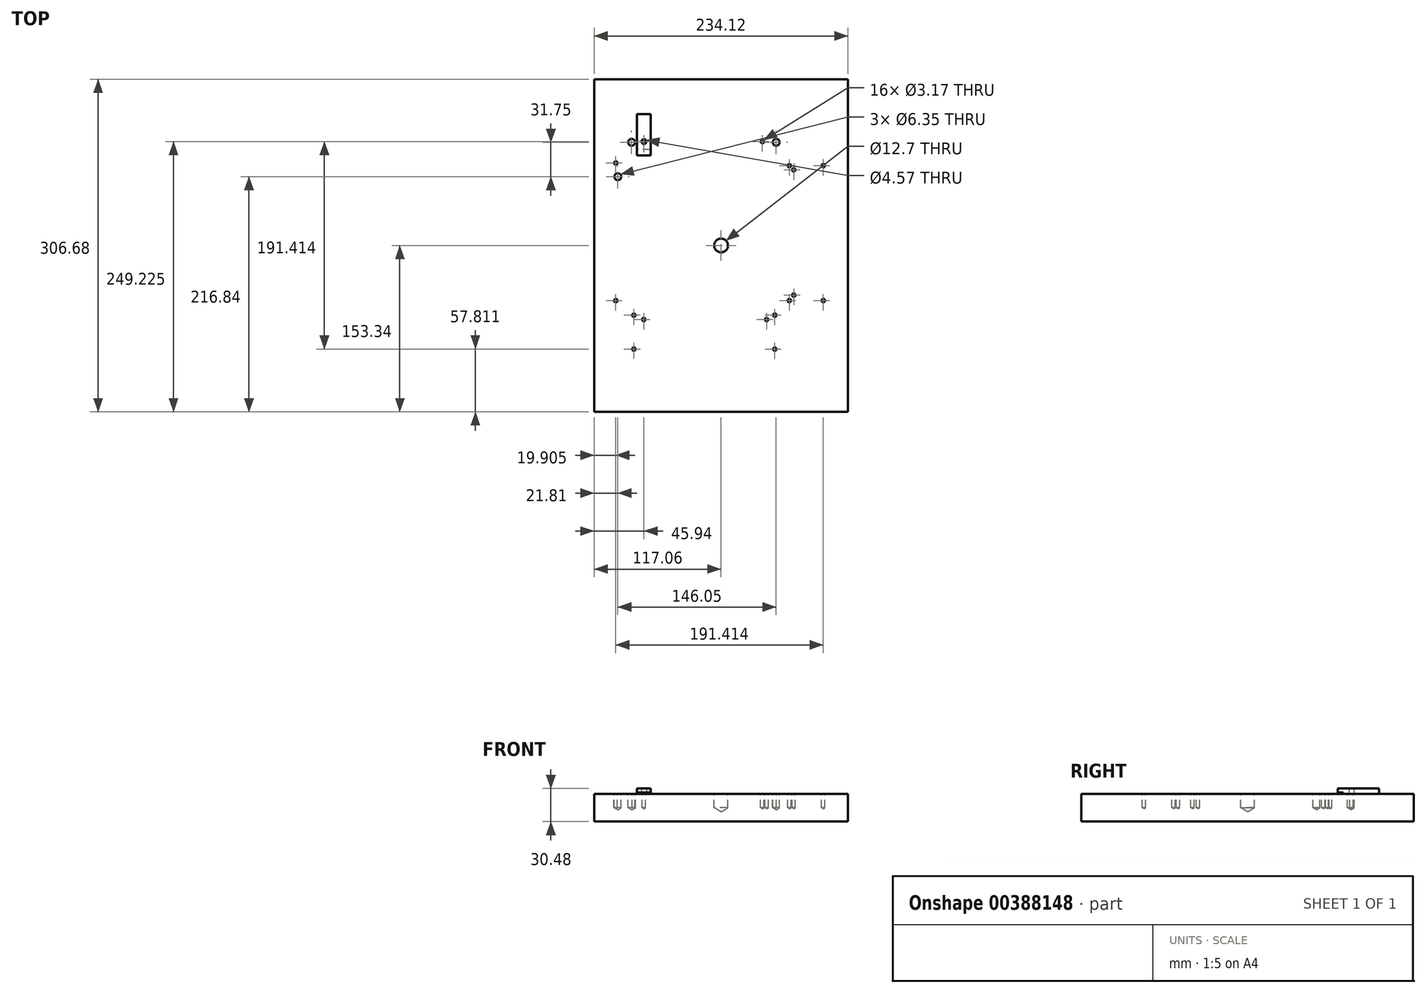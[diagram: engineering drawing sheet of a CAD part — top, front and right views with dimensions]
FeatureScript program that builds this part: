
annotation { "Feature Type Name" : "Feature", "Feature Type Description" : "" }
export const myFeature = defineFeature(function(context is Context, id is Id, definition is map)
    precondition{}
    {
        {
            var Q0;
            Q0=qCreatedBy(makeId("Top.planeOp"),FACE);
            var sketch = newSketch(context, id + "F0", { "sketchPlane" : qUnion([Q0])});
            skLineSegment(sketch, "E0.bottom", {"start": v(-117.06, 153.34) * mm, "end": v(117.06, 153.34) * mm});
            skLineSegment(sketch, "E0.top", {"start": v(-117.06, -153.34) * mm, "end": v(117.06, -153.34) * mm});
            skLineSegment(sketch, "E0.left", {"start": v(-117.06, 153.34) * mm, "end": v(-117.06, -153.34) * mm});
            skLineSegment(sketch, "E0.right", {"start": v(117.06, 153.34) * mm, "end": v(117.06, -153.34) * mm});
            skPoint(sketch, "E0.middle", {"position": v(0, 0) * mm});
            skPoint(sketch, "E1", {"position": v(-82.55, 95.25) * mm});
            skPoint(sketch, "E2", {"position": v(50.8, 95.25) * mm});
            skPoint(sketch, "E3", {"position": v(-95.25, 63.5) * mm});
            skPoint(sketch, "E4", {"position": v(-71.12, 95.88) * mm});
            skPoint(sketch, "E5", {"position": v(38.1, 95.89) * mm});
            skPoint(sketch, "E6", {"position": v(-97.16, 76.2) * mm});
            skPoint(sketch, "E7", {"position": v(-97.15, -50.8) * mm});
            skLineSegment(sketch, "E8", {"start": v(-97.16, 76.2) * mm, "end": v(-97.16, -50.8) * mm, "construction": true});
            skLineSegment(sketch, "E9", {"start": v(-71.12, 95.88) * mm, "end": v(38.1, 95.89) * mm, "construction": true});
            skLineSegment(sketch, "E10", {"start": v(62.94, 73.66) * mm, "end": v(62.94, -50.8) * mm, "construction": true});
            skLineSegment(sketch, "E11", {"start": v(67, 69.85) * mm, "end": v(67, -45.72) * mm, "construction": true});
            skLineSegment(sketch, "E12", {"start": v(94.26, 73.66) * mm, "end": v(94.26, -50.8) * mm, "construction": true});
            skLineSegment(sketch, "E13.bottom", {"start": v(-89.18, 87.9) * mm, "end": v(86.28, 87.9) * mm, "construction": true});
            skLineSegment(sketch, "E13.top", {"start": v(-89.18, -87.55) * mm, "end": v(86.28, -87.55) * mm, "construction": true});
            skLineSegment(sketch, "E13.left", {"start": v(-89.18, 87.9) * mm, "end": v(-89.18, -87.55) * mm, "construction": true});
            skLineSegment(sketch, "E13.right", {"start": v(86.28, 87.9) * mm, "end": v(86.28, -87.55) * mm, "construction": true});
            skLineSegment(sketch, "E14", {"start": v(59.03, 87.9) * mm, "end": v(59.03, -60.3) * mm, "construction": true});
            skLineSegment(sketch, "E15", {"start": v(59.03, -60.3) * mm, "end": v(-89.18, -60.3) * mm, "construction": true});
            skLineSegment(sketch, "E16", {"start": v(54.97, 87.9) * mm, "end": v(54.97, -56.24) * mm, "construction": true});
            skLineSegment(sketch, "E17", {"start": v(54.97, -56.24) * mm, "end": v(-89.18, -56.24) * mm, "construction": true});
            skPoint(sketch, "E18", {"position": v(62.94, 73.66) * mm});
            skPoint(sketch, "E19", {"position": v(67, 69.85) * mm});
            skPoint(sketch, "E20", {"position": v(94.26, 73.66) * mm});
            skPoint(sketch, "E21", {"position": v(62.94, -50.8) * mm});
            skPoint(sketch, "E22", {"position": v(67, -45.72) * mm});
            skPoint(sketch, "E23", {"position": v(94.26, -50.8) * mm});
            skLineSegment(sketch, "E24", {"start": v(-80.47, -64.21) * mm, "end": v(49.5, -64.21) * mm, "construction": true});
            skLineSegment(sketch, "E25", {"start": v(-71.33, -68.28) * mm, "end": v(42.03, -68.28) * mm, "construction": true});
            skLineSegment(sketch, "E26", {"start": v(-80.47, -95.53) * mm, "end": v(49.5, -95.53) * mm, "construction": true});
            skPoint(sketch, "E27", {"position": v(-80.47, -95.53) * mm});
            skPoint(sketch, "E28", {"position": v(-71.33, -68.28) * mm});
            skPoint(sketch, "E29", {"position": v(-80.47, -64.21) * mm});
            skPoint(sketch, "E30", {"position": v(49.5, -64.21) * mm});
            skPoint(sketch, "E31", {"position": v(42.03, -68.28) * mm});
            skPoint(sketch, "E32", {"position": v(49.5, -95.53) * mm});
            skCircle(sketch, "E33", {"center": v(-92.35, 91.08) * mm, "radius": 3.18 * mm, "construction": true});
            skCircle(sketch, "E34", {"center": v(-92.35, -59.41) * mm, "radius": 3.18 * mm, "construction": true});
            skCircle(sketch, "E35", {"center": v(-92.35, -90.73) * mm, "radius": 3.18 * mm, "construction": true});
            skCircle(sketch, "E36", {"center": v(-92.35, -63.47) * mm, "radius": 3.18 * mm, "construction": true});
            skCircle(sketch, "E37", {"center": v(58.14, -59.41) * mm, "radius": 3.18 * mm, "construction": true});
            skCircle(sketch, "E38", {"center": v(62.2, -63.47) * mm, "radius": 3.18 * mm, "construction": true});
            skCircle(sketch, "E39", {"center": v(89.46, -90.73) * mm, "radius": 3.18 * mm, "construction": true});
            skSolve(sketch);
        }
        {
            var Q0;
            Q0 = qSketchRegion(id + "F0", true);
            extrude(context, id + "F1", {"entities" : qUnion([Q0]), "oppositeDirection" : true, "depth" : 25.4 * mm});
        }
        {
            var Q0;
            Q0=sQuery(id+"F0.wireOp",VERTEX,"E1");
            var Q1;
            Q1=sQuery(id+"F0.wireOp",VERTEX,"E3");
            var Q2;
            Q2=sQuery(id+"F0.wireOp",VERTEX,"E2");
            var Q3;
            Q3=makeQuery(id+"F1.opExtrude","SWEPT_BODY",BODY,{"disambiguationData":[OSD([sQuery(id+"F0.wireOp",EDGE,"E0.bottom"),sQuery(id+"F0.wireOp",EDGE,"E0.top"),sQuery(id+"F0.wireOp",EDGE,"E0.left"),sQuery(id+"F0.wireOp",EDGE,"E0.right")])]});
            hole(context, id + "F2", {"style" : HoleStyle.SIMPLE, "endStyle" : HoleEndStyle.BLIND, "holeDiameter" : 6.35 * mm, "holeDepth" : 12.7 * mm, "isTappedThrough" : true, "tappedDepth" : 12.7 * mm, "tapClearance" : 3, "locations" : qUnion([Q0, Q1, Q2]), "scope" : qUnion([Q3])});
        }
        {
            var Q0;
            Q0=sQuery(id+"F0.wireOp",VERTEX,"E4");
            var Q1;
            Q1=sQuery(id+"F0.wireOp",VERTEX,"E5");
            var Q2;
            Q2=sQuery(id+"F0.wireOp",VERTEX,"E7");
            var Q3;
            Q3=sQuery(id+"F0.wireOp",VERTEX,"E6");
            var Q4;
            Q4=sQuery(id+"F0.wireOp",VERTEX,"E18");
            var Q5;
            Q5=sQuery(id+"F0.wireOp",VERTEX,"E19");
            var Q6;
            Q6=sQuery(id+"F0.wireOp",VERTEX,"E20");
            var Q7;
            Q7=sQuery(id+"F0.wireOp",VERTEX,"E21");
            var Q8;
            Q8=sQuery(id+"F0.wireOp",VERTEX,"E22");
            var Q9;
            Q9=sQuery(id+"F0.wireOp",VERTEX,"E23");
            var Q10;
            Q10=sQuery(id+"F0.wireOp",VERTEX,"E29");
            var Q11;
            Q11=sQuery(id+"F0.wireOp",VERTEX,"E28");
            var Q12;
            Q12=sQuery(id+"F0.wireOp",VERTEX,"E27");
            var Q13;
            Q13=sQuery(id+"F0.wireOp",VERTEX,"E32");
            var Q14;
            Q14=sQuery(id+"F0.wireOp",VERTEX,"E31");
            var Q15;
            Q15=sQuery(id+"F0.wireOp",VERTEX,"E30");
            var Q16;
            Q16=makeQuery(id+"F1.opExtrude","SWEPT_BODY",BODY,{"disambiguationData":[OSD([sQuery(id+"F0.wireOp",EDGE,"E0.bottom"),sQuery(id+"F0.wireOp",EDGE,"E0.top"),sQuery(id+"F0.wireOp",EDGE,"E0.left"),sQuery(id+"F0.wireOp",EDGE,"E0.right")])]});
            hole(context, id + "F3", {"style" : HoleStyle.SIMPLE, "endStyle" : HoleEndStyle.BLIND, "holeDiameter" : 3.17 * mm, "holeDepth" : 12.7 * mm, "isTappedThrough" : true, "tappedDepth" : 12.7 * mm, "tapClearance" : 3, "locations" : qUnion([Q0, Q1, Q2, Q3, Q4, Q5, Q6, Q7, Q8, Q9, Q10, Q11, Q12, Q13, Q14, Q15]), "scope" : qUnion([Q16])});
        }
        {
            var Q0;
            Q0=makeQuery(id+"F0.imprint","IMPRINT",FACE,{"disambiguationData":[TD([[makeQuery(id+"F0.imprint","IMPRINT",EDGE,{"derivedFrom":sQuery(id+"F0.wireOp",EDGE,"E0.bottom")}),-1.0]])]});
            var sketch = newSketch(context, id + "F4", { "sketchPlane" : qUnion([Q0])});
            skLineSegment(sketch, "E40.bottom", {"start": v(-77.47, 121.29) * mm, "end": v(-64.77, 121.29) * mm});
            skLineSegment(sketch, "E40.top", {"start": v(-77.47, 83.18) * mm, "end": v(-64.77, 83.18) * mm});
            skLineSegment(sketch, "E40.left", {"start": v(-77.47, 121.29) * mm, "end": v(-77.47, 83.18) * mm});
            skLineSegment(sketch, "E40.right", {"start": v(-64.77, 121.29) * mm, "end": v(-64.77, 83.18) * mm});
            skCircle(sketch, "E41", {"center": v(-71.12, 95.88) * mm, "radius": 2.29 * mm});
            skPoint(sketch, "E42", {"position": v(-71.12, 83.18) * mm});
            skSolve(sketch);
        }
        {
            var Q0;
            Q0 = qSketchRegion(id + "F4", true);
            extrude(context, id + "F5", {"entities" : qUnion([Q0]), "depth" : 5.08 * mm});
        }
        {
            var Q0;
            Q0=makeQuery(id+"F5.opExtrude","CAP_FACE",FACE,{"disambiguationData":[OSD([sQuery(id+"F4.wireOp",EDGE,"E40.bottom"),sQuery(id+"F4.wireOp",EDGE,"E40.top"),sQuery(id+"F4.wireOp",EDGE,"E40.left"),sQuery(id+"F4.wireOp",EDGE,"E40.right"),sQuery(id+"F4.wireOp",EDGE,"E41")])],"isStart":true});
            var sketch = newSketch(context, id + "F6", { "sketchPlane" : qUnion([Q0])});
            skLineSegment(sketch, "E43.bottom", {"start": v(-64.77, -83.18) * mm, "end": v(-77.47, -83.18) * mm});
            skLineSegment(sketch, "E43.top", {"start": v(-64.77, -88.42) * mm, "end": v(-77.47, -88.42) * mm});
            skLineSegment(sketch, "E43.left", {"start": v(-64.77, -83.18) * mm, "end": v(-64.77, -88.42) * mm});
            skLineSegment(sketch, "E43.right", {"start": v(-77.47, -83.18) * mm, "end": v(-77.47, -88.42) * mm});
            skSolve(sketch);
        }
        {
            var Q0;
            Q0 = qSketchRegion(id + "F6", true);
            extrude(context, id + "F7", {"entities" : qUnion([Q0]), "operationType" : NewBodyOperationType.REMOVE, "oppositeDirection" : true, "depth" : 1.27 * mm});
        }
        {
            var Q0;
            Q0=sQuery(id+"F0.wireOp",VERTEX,"E0.middle");
            var Q1;
            Q1=makeQuery(id+"F1.opExtrude","SWEPT_BODY",BODY,{"disambiguationData":[OSD([sQuery(id+"F0.wireOp",EDGE,"E0.bottom"),sQuery(id+"F0.wireOp",EDGE,"E0.top"),sQuery(id+"F0.wireOp",EDGE,"E0.left"),sQuery(id+"F0.wireOp",EDGE,"E0.right")])]});
            hole(context, id + "F8", {"style" : HoleStyle.SIMPLE, "endStyle" : HoleEndStyle.BLIND, "holeDiameter" : 12.7 * mm, "holeDepth" : 12.7 * mm, "isTappedThrough" : true, "tappedDepth" : 12.7 * mm, "tapClearance" : 3, "locations" : qUnion([Q0]), "scope" : qUnion([Q1])});
        }
    });
